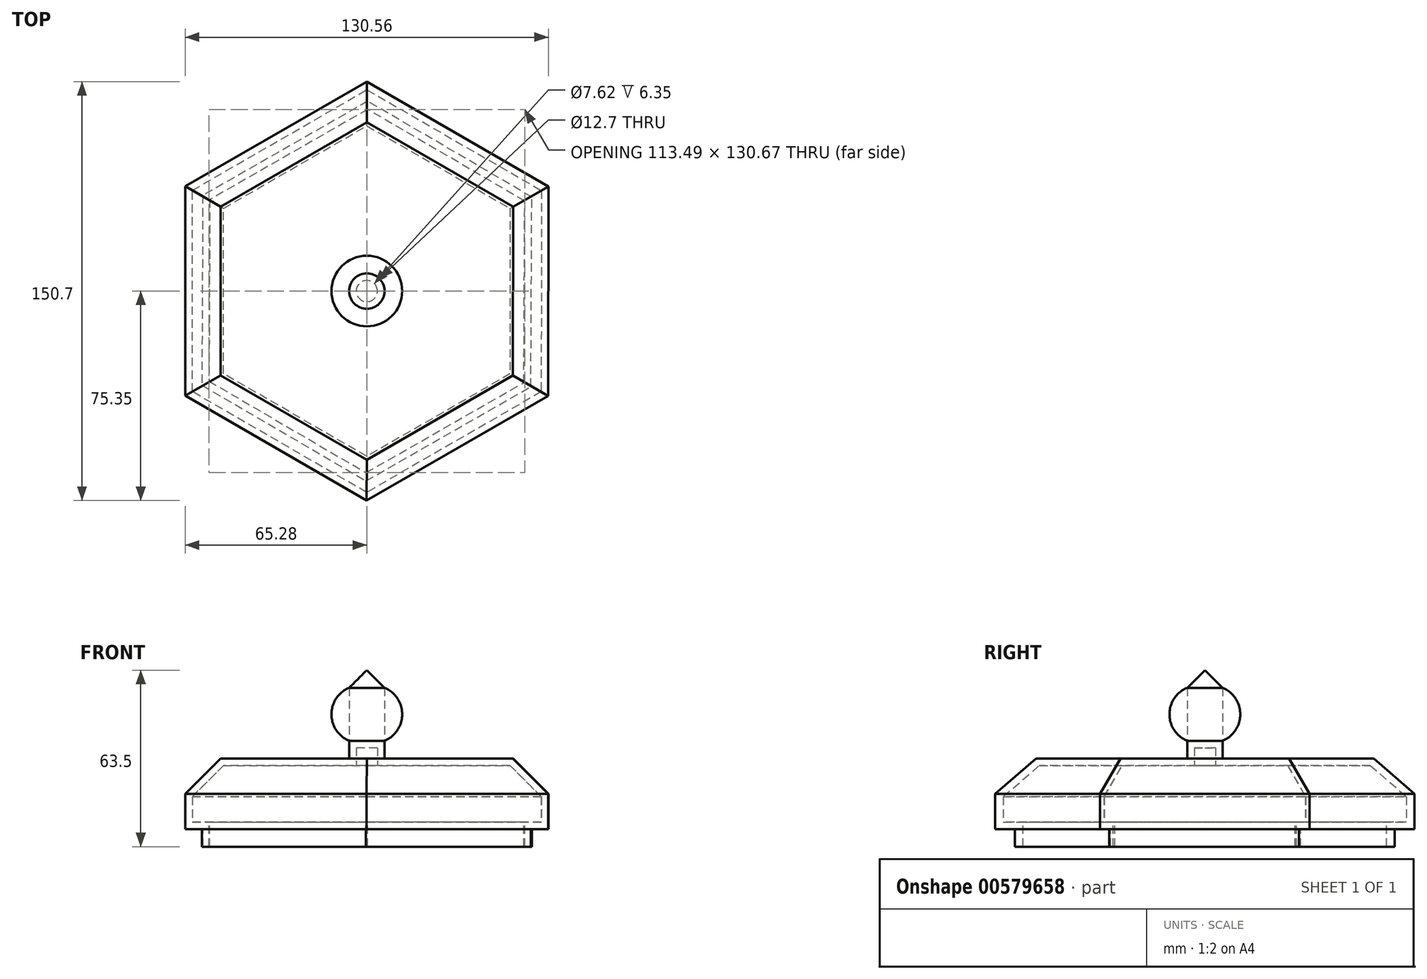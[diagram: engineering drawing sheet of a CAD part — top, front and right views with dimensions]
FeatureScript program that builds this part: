
annotation { "Feature Type Name" : "Feature", "Feature Type Description" : "" }
export const myFeature = defineFeature(function(context is Context, id is Id, definition is map)
    precondition{}
    {
        {
            var Q0;
            Q0=qCreatedBy(makeId("Top.planeOp"),FACE);
            var sketch = newSketch(context, id + "F0", { "sketchPlane" : qUnion([Q0])});
            skCircle(sketch, "E0.cCircle", {"center": v(0, 0) * mm, "radius": 65.25 * mm, "construction": true});
            skLineSegment(sketch, "E0.0", {"start": v(65.23, -37.72) * mm, "end": v(-0.05, -75.35) * mm});
            skLineSegment(sketch, "E0.1", {"start": v(-0.05, -75.35) * mm, "end": v(-65.28, -37.63) * mm});
            skLineSegment(sketch, "E0.2", {"start": v(-65.28, -37.63) * mm, "end": v(-65.23, 37.72) * mm});
            skLineSegment(sketch, "E0.3", {"start": v(-65.23, 37.72) * mm, "end": v(0.05, 75.35) * mm});
            skLineSegment(sketch, "E0.4", {"start": v(0.05, 75.35) * mm, "end": v(65.28, 37.63) * mm});
            skLineSegment(sketch, "E0.5", {"start": v(65.28, 37.63) * mm, "end": v(65.23, -37.72) * mm});
            skPoint(sketch, "E0.0.midPoint", {"position": v(32.6, -56.53) * mm});
            skSolve(sketch);
        }
        {
            var Q0;
            Q0=makeQuery(id+"F0.imprint","IMPRINT",FACE,{"disambiguationData":[TD([[makeQuery(id+"F0.imprint","IMPRINT",EDGE,{"derivedFrom":sQuery(id+"F0.wireOp",EDGE,"E0.0")}),-1.0]])]});
            extrude(context, id + "F1", {"entities" : qUnion([Q0]), "depth" : 25.4 * mm, "offsetDistance" : 25.4 * mm});
        }
        {
            var Q0;
            Q0=makeQuery(id+"F1.opExtrude","CAP_FACE",FACE,{"disambiguationData":[OSD([sQuery(id+"F0.wireOp",EDGE,"E0.0"),sQuery(id+"F0.wireOp",EDGE,"E0.1"),sQuery(id+"F0.wireOp",EDGE,"E0.2"),sQuery(id+"F0.wireOp",EDGE,"E0.3"),sQuery(id+"F0.wireOp",EDGE,"E0.4"),sQuery(id+"F0.wireOp",EDGE,"E0.5")])],"isStart":false});
            chamfer(context, id + "F2", {"entities" : qUnion([Q0]), "width" : 12.7 * mm, "tangentPropagation" : true});
        }
        {
            var Q0;
            Q0=makeQuery(id+"F1.opExtrude","CAP_FACE",FACE,{"disambiguationData":[OSD([sQuery(id+"F0.wireOp",EDGE,"E0.0"),sQuery(id+"F0.wireOp",EDGE,"E0.1"),sQuery(id+"F0.wireOp",EDGE,"E0.2"),sQuery(id+"F0.wireOp",EDGE,"E0.3"),sQuery(id+"F0.wireOp",EDGE,"E0.4"),sQuery(id+"F0.wireOp",EDGE,"E0.5")])],"isStart":false});
            var sketch = newSketch(context, id + "F3", { "sketchPlane" : qUnion([Q0])});
            skCircle(sketch, "E1", {"center": v(0, 0) * mm, "radius": 6.35 * mm});
            skSolve(sketch);
        }
        {
            var Q0;
            Q0=makeQuery(id+"F3.imprint","IMPRINT",FACE,{"disambiguationData":[TD([[makeQuery(id+"F3.imprint","IMPRINT",EDGE,{"derivedFrom":sQuery(id+"F3.wireOp",EDGE,"E1")}),1.0]])]});
            extrude(context, id + "F4", {"entities" : qUnion([Q0]), "operationType" : NewBodyOperationType.ADD, "depth" : 6.35 * mm, "offsetDistance" : 25.4 * mm});
        }
        {
            var Q0;
            Q0=makeQuery(id+"F4.opExtrude","CAP_FACE",FACE,{"disambiguationData":[OSD([sQuery(id+"F3.wireOp",EDGE,"E1")])],"isStart":false});
            var sketch = newSketch(context, id + "F5", { "sketchPlane" : qUnion([Q0])});
            skCircle(sketch, "E2", {"center": v(0, 0) * mm, "radius": 12.7 * mm});
            skSolve(sketch);
        }
        {
            var Q0;
            Q0=makeQuery(id+"F5.imprint","IMPRINT",FACE,{"disambiguationData":[TD([[makeQuery(id+"F5.imprint","IMPRINT",EDGE,{"derivedFrom":sQuery(id+"F5.wireOp",EDGE,"E2")}),1.0]])]});
            extrude(context, id + "F6", {"entities" : qUnion([Q0]), "depth" : 19.05 * mm, "offsetDistance" : 25.4 * mm});
        }
        {
            var Q0;
            Q0=makeQuery(id+"F6.opExtrude","CAP_EDGE",EDGE,{"disambiguationData":[OSD([sQuery(id+"F5.wireOp",EDGE,"E2")])],"isStart":false});
            var Q1;
            Q1=makeQuery(id+"F6.opExtrude","CAP_EDGE",EDGE,{"disambiguationData":[OSD([sQuery(id+"F5.wireOp",EDGE,"E2")])],"isStart":true});
            fillet(context, id + "F7", {"entities" : qUnion([Q0, Q1]), "radius" : 10.16 * mm, "tangentPropagation" : true, "allowEdgeOverflow" : false});
        }
        {
            var Q0;
            Q0=makeQuery(id+"F4.opExtrude","CAP_FACE",FACE,{"disambiguationData":[OSD([sQuery(id+"F3.wireOp",EDGE,"E1")])],"isStart":false});
            extrude(context, id + "F8", {"entities" : qUnion([Q0]), "depth" : 25.4 * mm, "offsetDistance" : 25.4 * mm});
        }
        {
            var Q0;
            Q0=makeQuery(id+"F8.opExtrude","CAP_EDGE",EDGE,{"disambiguationData":[OSD([sQuery(id+"F3.wireOp",EDGE,"E1")])],"isStart":false});
            chamfer(context, id + "F9", {"entities" : qUnion([Q0]), "width" : 6.35 * mm, "tangentPropagation" : true});
        }
        {
            var Q0;
            Q0=makeQuery(id+"F1.opExtrude","CAP_FACE",FACE,{"disambiguationData":[OSD([sQuery(id+"F0.wireOp",EDGE,"E0.0"),sQuery(id+"F0.wireOp",EDGE,"E0.1"),sQuery(id+"F0.wireOp",EDGE,"E0.2"),sQuery(id+"F0.wireOp",EDGE,"E0.3"),sQuery(id+"F0.wireOp",EDGE,"E0.4"),sQuery(id+"F0.wireOp",EDGE,"E0.5")])],"isStart":true});
            var sketch = newSketch(context, id + "F10", { "sketchPlane" : qUnion([Q0])});
            skCircle(sketch, "E3.cCircle", {"center": v(0, 0) * mm, "radius": 59.12 * mm, "construction": true});
            skLineSegment(sketch, "E3.0", {"start": v(-0.34, 68.27) * mm, "end": v(58.96, 34.43) * mm});
            skLineSegment(sketch, "E3.1", {"start": v(58.96, 34.43) * mm, "end": v(59.3, -33.84) * mm});
            skLineSegment(sketch, "E3.2", {"start": v(59.3, -33.84) * mm, "end": v(0.34, -68.27) * mm});
            skLineSegment(sketch, "E3.3", {"start": v(0.34, -68.27) * mm, "end": v(-58.96, -34.43) * mm});
            skLineSegment(sketch, "E3.4", {"start": v(-58.96, -34.43) * mm, "end": v(-59.3, 33.84) * mm});
            skLineSegment(sketch, "E3.5", {"start": v(-59.3, 33.84) * mm, "end": v(-0.34, 68.27) * mm});
            skPoint(sketch, "E3.0.midPoint", {"position": v(29.3, 51.35) * mm});
            skSolve(sketch);
        }
        {
            var Q0;
            Q0=makeQuery(id+"F10.imprint","IMPRINT",FACE,{"disambiguationData":[TD([[makeQuery(id+"F10.imprint","IMPRINT",EDGE,{"derivedFrom":sQuery(id+"F10.wireOp",EDGE,"E3.0")}),-1.0]])]});
            extrude(context, id + "F11", {"entities" : qUnion([Q0]), "operationType" : NewBodyOperationType.ADD, "depth" : 6.35 * mm, "offsetDistance" : 25.4 * mm});
        }
        {
            var Q0;
            Q0=makeQuery(id+"F11.opExtrude","CAP_FACE",FACE,{"disambiguationData":[OSD([sQuery(id+"F10.wireOp",EDGE,"E3.0"),sQuery(id+"F10.wireOp",EDGE,"E3.1"),sQuery(id+"F10.wireOp",EDGE,"E3.2"),sQuery(id+"F10.wireOp",EDGE,"E3.3"),sQuery(id+"F10.wireOp",EDGE,"E3.4"),sQuery(id+"F10.wireOp",EDGE,"E3.5")])],"isStart":false});
            shell(context, id + "F12", {"entities" : qUnion([Q0]), "thickness" : 2.54 * mm});
        }
    });
